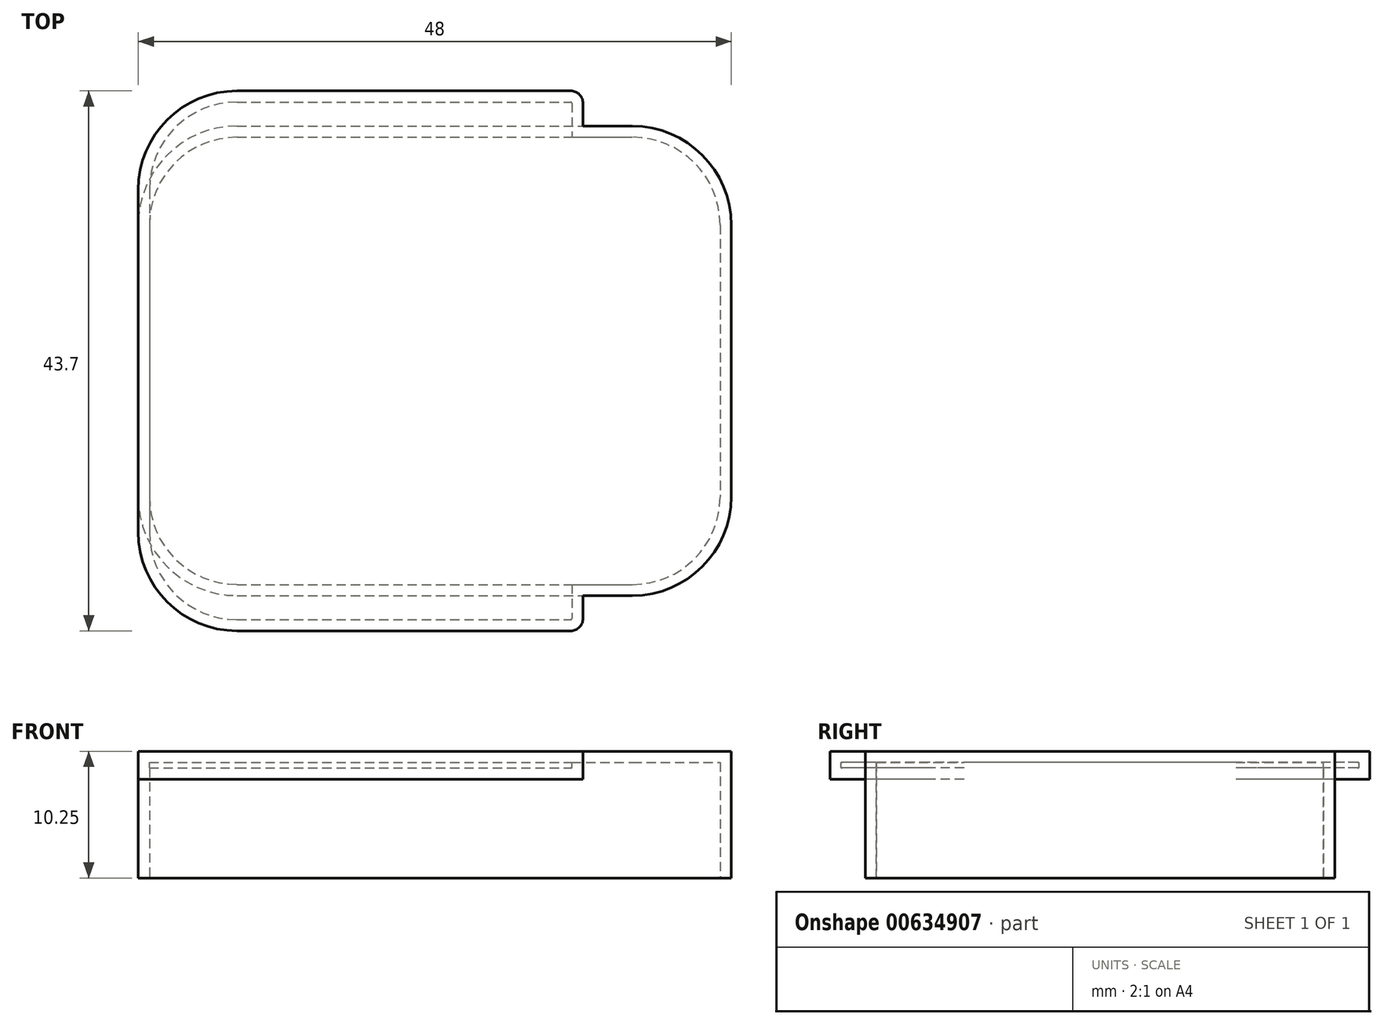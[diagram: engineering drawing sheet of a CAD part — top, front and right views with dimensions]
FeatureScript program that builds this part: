
annotation { "Feature Type Name" : "Feature", "Feature Type Description" : "" }
export const myFeature = defineFeature(function(context is Context, id is Id, definition is map)
    precondition{}
    {
        {
            var Q0;
            Q0=qCreatedBy(makeId("Top.planeOp"),FACE);
            var sketch = newSketch(context, id + "F0", { "sketchPlane" : qUnion([Q0])});
            skLineSegment(sketch, "E0.bottom", {"start": v(-16, 19) * mm, "end": v(16, 19) * mm});
            skLineSegment(sketch, "E0.top", {"start": v(-16, -19) * mm, "end": v(16, -19) * mm});
            skLineSegment(sketch, "E0.left", {"start": v(-24, 11) * mm, "end": v(-24, -11) * mm});
            skLineSegment(sketch, "E0.right", {"start": v(24, 11) * mm, "end": v(24, -11) * mm});
            skPoint(sketch, "E1.visualSharp", {"position": v(24, 19) * mm});
            skArc(sketch, "E1.filletArc", {"start": v(24, 11) * mm, "mid": v(21.66, 16.66) * mm, "end": v(16, 19) * mm});
            skPoint(sketch, "E2.visualSharp", {"position": v(24, -19) * mm});
            skArc(sketch, "E2.filletArc", {"start": v(16, -19) * mm, "mid": v(21.66, -16.66) * mm, "end": v(24, -11) * mm});
            skPoint(sketch, "E3.visualSharp", {"position": v(-24, -19) * mm});
            skArc(sketch, "E3.filletArc", {"start": v(-24, -11) * mm, "mid": v(-21.66, -16.66) * mm, "end": v(-16, -19) * mm});
            skPoint(sketch, "E4.visualSharp", {"position": v(-24, 19) * mm});
            skArc(sketch, "E4.filletArc", {"start": v(-16, 19) * mm, "mid": v(-21.66, 16.66) * mm, "end": v(-24, 11) * mm});
            skSolve(sketch);
        }
        {
            var Q0;
            Q0=makeQuery(id+"F0.imprint","IMPRINT",FACE,{"disambiguationData":[TD([[makeQuery(id+"F0.imprint","IMPRINT",EDGE,{"derivedFrom":sQuery(id+"F0.wireOp",EDGE,"E0.bottom")}),-1.0]])]});
            extrude(context, id + "F1", {"entities" : qUnion([Q0]), "depth" : 10.25 * mm, "offsetDistance" : 25 * mm});
        }
        {
            var Q0;
            Q0=makeQuery(id+"F1.opExtrude","CAP_FACE",FACE,{"disambiguationData":[OSD([sQuery(id+"F0.wireOp",EDGE,"E0.bottom"),sQuery(id+"F0.wireOp",EDGE,"E0.top"),sQuery(id+"F0.wireOp",EDGE,"E0.left"),sQuery(id+"F0.wireOp",EDGE,"E0.right"),sQuery(id+"F0.wireOp",EDGE,"E1.filletArc"),sQuery(id+"F0.wireOp",EDGE,"E2.filletArc"),sQuery(id+"F0.wireOp",EDGE,"E3.filletArc"),sQuery(id+"F0.wireOp",EDGE,"E4.filletArc")])],"isStart":false});
            var sketch = newSketch(context, id + "F2", { "sketchPlane" : qUnion([Q0])});
            skPoint(sketch, "E5.firstSnap0", {"position": v(-24, 0) * mm});
            skLineSegment(sketch, "E5.bottom", {"start": v(-16, 21.85) * mm, "end": v(12, 21.85) * mm});
            skLineSegment(sketch, "E5.top", {"start": v(-16, -21.85) * mm, "end": v(12, -21.85) * mm});
            skLineSegment(sketch, "E5.left", {"start": v(-24, 13.85) * mm, "end": v(-24, -13.85) * mm});
            skLineSegment(sketch, "E5.right", {"start": v(12, 21.85) * mm, "end": v(12, -21.85) * mm});
            skPoint(sketch, "E6.visualSharp", {"position": v(-24, 21.85) * mm});
            skArc(sketch, "E6.filletArc", {"start": v(-16, 21.85) * mm, "mid": v(-21.66, 19.5) * mm, "end": v(-24, 13.85) * mm});
            skPoint(sketch, "E7.visualSharp", {"position": v(-24, -21.85) * mm});
            skArc(sketch, "E7.filletArc", {"start": v(-24, -13.85) * mm, "mid": v(-21.66, -19.5) * mm, "end": v(-16, -21.85) * mm});
            skSolve(sketch);
        }
        {
            var Q0;
            {var subQ1=sQuery(id+"F2.wireOp",EDGE,"E5.top");Q0=makeQuery(id+"F2.imprint","IMPRINT",FACE,{"disambiguationData":[TD([[makeQuery(id+"F2.imprint","IMPRINT",EDGE,{"derivedFrom":subQ1}),1.0]])]});}
            var Q1;
            {var subQ4=sQuery(id+"F2.wireOp",EDGE,"E5.bottom");Q1=makeQuery(id+"F2.imprint","IMPRINT",FACE,{"disambiguationData":[TD([[makeQuery(id+"F2.imprint","IMPRINT",EDGE,{"derivedFrom":subQ4}),-1.0]])]});}
            extrude(context, id + "F3", {"entities" : qUnion([Q0, Q1]), "operationType" : NewBodyOperationType.ADD, "oppositeDirection" : true, "depth" : 2.25 * mm, "offsetDistance" : 25 * mm});
        }
        {
            var Q0;
            Q0=makeQuery(id+"F3.opExtrude","SWEPT_EDGE",EDGE,{"disambiguationData":[OSD([sQuery(id+"F2.wireOp",EDGE,"E5.top"),sQuery(id+"F2.wireOp",EDGE,"E5.right")])]});
            var Q1;
            Q1=makeQuery(id+"F3.opExtrude","SWEPT_EDGE",EDGE,{"disambiguationData":[OSD([sQuery(id+"F2.wireOp",EDGE,"E5.bottom"),sQuery(id+"F2.wireOp",EDGE,"E5.right")])]});
            var Q2;
            Q2=makeQuery(id+"F3.opExtrude","SWEPT_EDGE",EDGE,{"disambiguationData":[OSD([sQuery(id+"F0.wireOp",EDGE,"E0.bottom"),sQuery(id+"F2.wireOp",EDGE,"E5.right")])]});
            var Q3;
            Q3=makeQuery(id+"F3.opExtrude","SWEPT_EDGE",EDGE,{"disambiguationData":[OSD([sQuery(id+"F0.wireOp",EDGE,"E0.top"),sQuery(id+"F2.wireOp",EDGE,"E5.right")])]});
            fillet(context, id + "F4", {"entities" : qUnion([Q0, Q1, Q2, Q3]), "radius" : 1 * mm, "tangentPropagation" : true, "allowEdgeOverflow" : false});
        }
        {
            var Q0;
            Q0=makeQuery(id+"F1.opExtrude","CAP_FACE",FACE,{"disambiguationData":[OSD([sQuery(id+"F0.wireOp",EDGE,"E0.bottom"),sQuery(id+"F0.wireOp",EDGE,"E0.top"),sQuery(id+"F0.wireOp",EDGE,"E0.left"),sQuery(id+"F0.wireOp",EDGE,"E0.right"),sQuery(id+"F0.wireOp",EDGE,"E1.filletArc"),sQuery(id+"F0.wireOp",EDGE,"E2.filletArc"),sQuery(id+"F0.wireOp",EDGE,"E3.filletArc"),sQuery(id+"F0.wireOp",EDGE,"E4.filletArc")])],"isStart":true});
            shell(context, id + "F5", {"entities" : qUnion([Q0]), "thickness" : 0.9 * mm});
        }
    });
